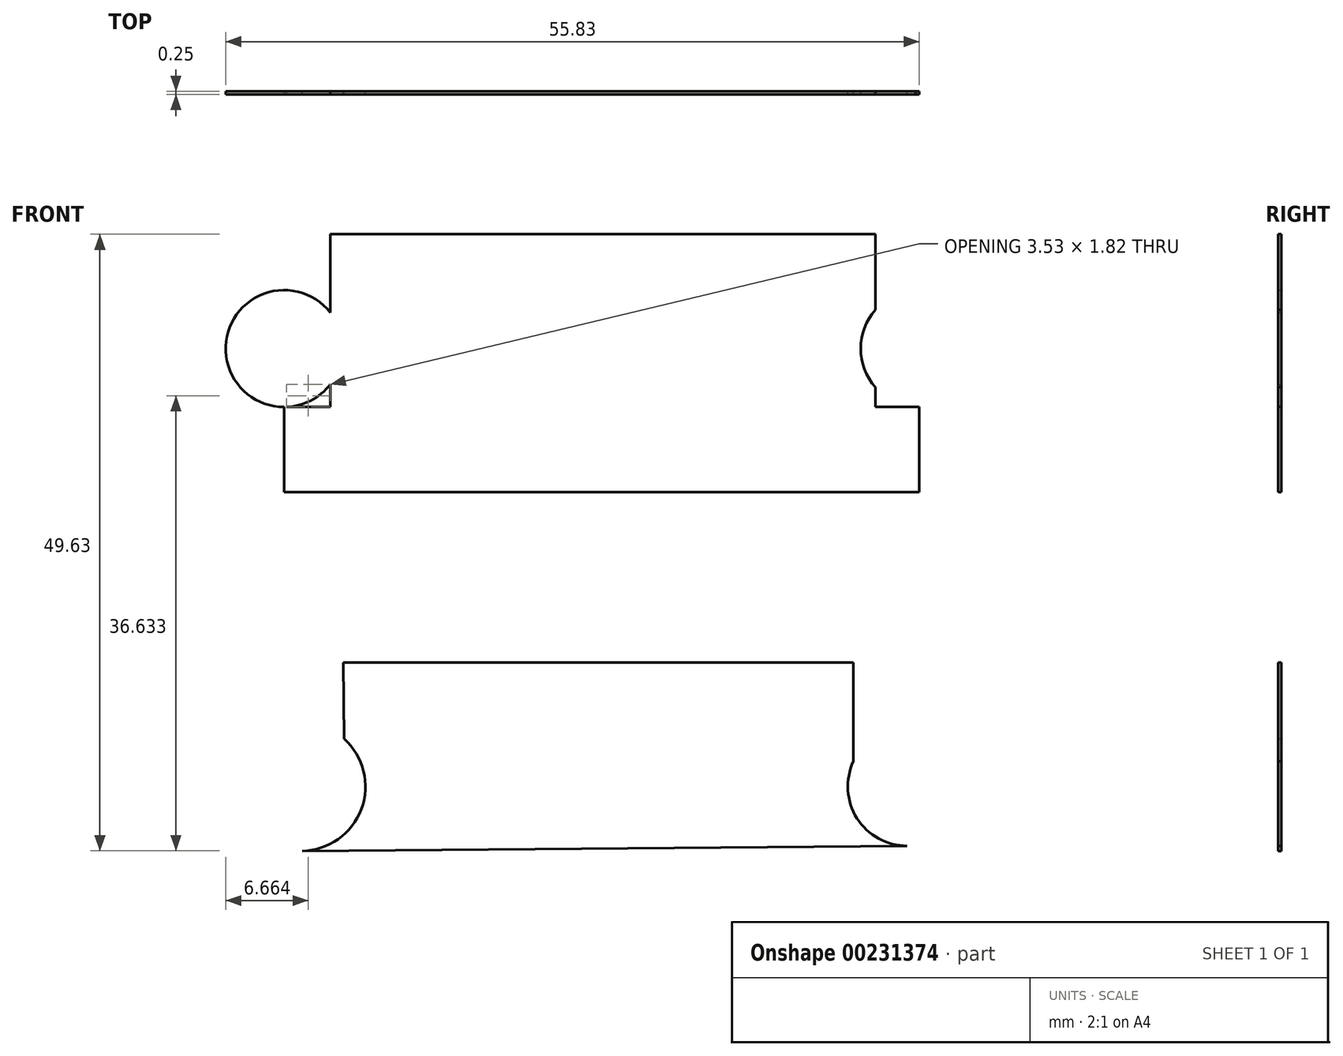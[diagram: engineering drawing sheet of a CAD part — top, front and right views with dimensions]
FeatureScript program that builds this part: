
annotation { "Feature Type Name" : "Feature", "Feature Type Description" : "" }
export const myFeature = defineFeature(function(context is Context, id is Id, definition is map)
    precondition{}
    {
        {
            var Q0;
            Q0=qCreatedBy(makeId("Front.planeOp"),FACE);
            var sketch = newSketch(context, id + "F0", { "sketchPlane" : qUnion([Q0])});
            skLineSegment(sketch, "E0.top", {"start": v(-21.15, -11.26) * mm, "end": v(27.62, -11.26) * mm});
            skLineSegment(sketch, "E0.left", {"start": v(-21.15, -1.36) * mm, "end": v(-21.15, -11.26) * mm});
            skLineSegment(sketch, "E0.right", {"start": v(27.62, -0.95) * mm, "end": v(27.62, -11.26) * mm});
            skCircle(sketch, "E1", {"center": v(-21.15, 3.82) * mm, "radius": 5.17 * mm});
            skCircle(sketch, "E2", {"center": v(27.62, 3.82) * mm, "radius": 4.77 * mm});
            skLineSegment(sketch, "E3", {"start": v(-21.15, -1.36) * mm, "end": v(27.62, -0.95) * mm});
            skLineSegment(sketch, "E4", {"start": v(-17.7, 7.67) * mm, "end": v(-17.75, 13.8) * mm});
            skLineSegment(sketch, "E5", {"start": v(-17.75, 13.8) * mm, "end": v(23.3, 13.8) * mm});
            skLineSegment(sketch, "E6", {"start": v(23.3, 13.8) * mm, "end": v(23.3, 5.85) * mm});
            skLineSegment(sketch, "E7.bottom", {"start": v(-22.52, 8.81) * mm, "end": v(-20.17, 8.81) * mm});
            skLineSegment(sketch, "E7.top", {"start": v(-22.52, 27.52) * mm, "end": v(-20.17, 27.52) * mm});
            skLineSegment(sketch, "E7.left", {"start": v(-22.52, 8.81) * mm, "end": v(-22.52, 27.52) * mm});
            skLineSegment(sketch, "E7.right", {"start": v(-20.17, 8.81) * mm, "end": v(-20.17, 27.52) * mm});
            skLineSegment(sketch, "E8.bottom", {"start": v(26.65, 8.48) * mm, "end": v(28.6, 8.48) * mm});
            skLineSegment(sketch, "E8.top", {"start": v(26.65, 27.13) * mm, "end": v(28.6, 27.13) * mm});
            skLineSegment(sketch, "E8.left", {"start": v(26.65, 8.48) * mm, "end": v(26.65, 27.13) * mm});
            skLineSegment(sketch, "E8.right", {"start": v(28.6, 8.48) * mm, "end": v(28.6, 27.13) * mm});
            skLineSegment(sketch, "E9.bottom", {"start": v(-22.52, 27.52) * mm, "end": v(28.6, 27.52) * mm});
            skLineSegment(sketch, "E9.left", {"start": v(-22.52, 27.52) * mm, "end": v(-22.52, 34.37) * mm});
            skLineSegment(sketch, "E9.right", {"start": v(28.6, 27.52) * mm, "end": v(28.6, 34.37) * mm});
            skCircle(sketch, "E10", {"center": v(-22.52, 39.07) * mm, "radius": 4.7 * mm});
            skCircle(sketch, "E11", {"center": v(28.6, 39.07) * mm, "radius": 4.7 * mm});
            skLineSegment(sketch, "E12", {"start": v(-22.33, 34.37) * mm, "end": v(28.32, 34.37) * mm});
            skLineSegment(sketch, "E13", {"start": v(-18.8, 34.37) * mm, "end": v(-18.8, 36.2) * mm});
            skLineSegment(sketch, "E14", {"start": v(-18.8, 48.28) * mm, "end": v(25.07, 48.28) * mm});
            skLineSegment(sketch, "E15", {"start": v(25.07, 48.28) * mm, "end": v(25.07, 42.19) * mm});
            skLineSegment(sketch, "E16.trimOffspring", {"start": v(-18.8, 41.96) * mm, "end": v(-18.8, 48.28) * mm});
            skLineSegment(sketch, "E17.trimOffspring", {"start": v(25.07, 35.96) * mm, "end": v(25.07, 34.37) * mm});
            skSolve(sketch);
        }
        {
            var Q0;
            {var subQ0=sQuery(id+"F0.wireOp",EDGE,"E4");Q0=makeQuery(id+"F0.imprint","IMPRINT",FACE,{"disambiguationData":[TD([[makeQuery(id+"F0.imprint","IMPRINT",EDGE,{"derivedFrom":subQ0}),-1.0]])]});}
            var Q1;
            {var subQ0=sQuery(id+"F0.wireOp",EDGE,"E13");Q1=makeQuery(id+"F0.imprint","IMPRINT",FACE,{"disambiguationData":[TD([[makeQuery(id+"F0.imprint","IMPRINT",EDGE,{"derivedFrom":subQ0}),-1.0]])]});}
            var Q2;
            {var subQ5=sQuery(id+"F0.wireOp",EDGE,"E9.left");Q2=makeQuery(id+"F0.imprint","IMPRINT",FACE,{"disambiguationData":[TD([[makeQuery(id+"F0.imprint","IMPRINT",EDGE,{"derivedFrom":subQ5}),-1.0]])]});}
            var Q3;
            {var subQ0=sQuery(id+"F0.wireOp",EDGE,"E10");var subQ1=makeQuery(id+"F0.imprint","INTERSECT",VERTEX,{"derivedFrom":[sQuery(id+"F0.wireOp",EDGE,"E9.left"),subQ0]});Q3=makeQuery(id+"F0.imprint","IMPRINT",FACE,{"disambiguationData":[TD([[makeQuery(id+"F0.imprint","IMPRINT",EDGE,{"disambiguationData":[TD([[subQ1,1.0]])],"derivedFrom":subQ0}),1.0]])]});}
            extrude(context, id + "F1", {"entities" : qUnion([Q0, Q1, Q2, Q3]), "depth" : 0.25 * mm});
        }
    });
